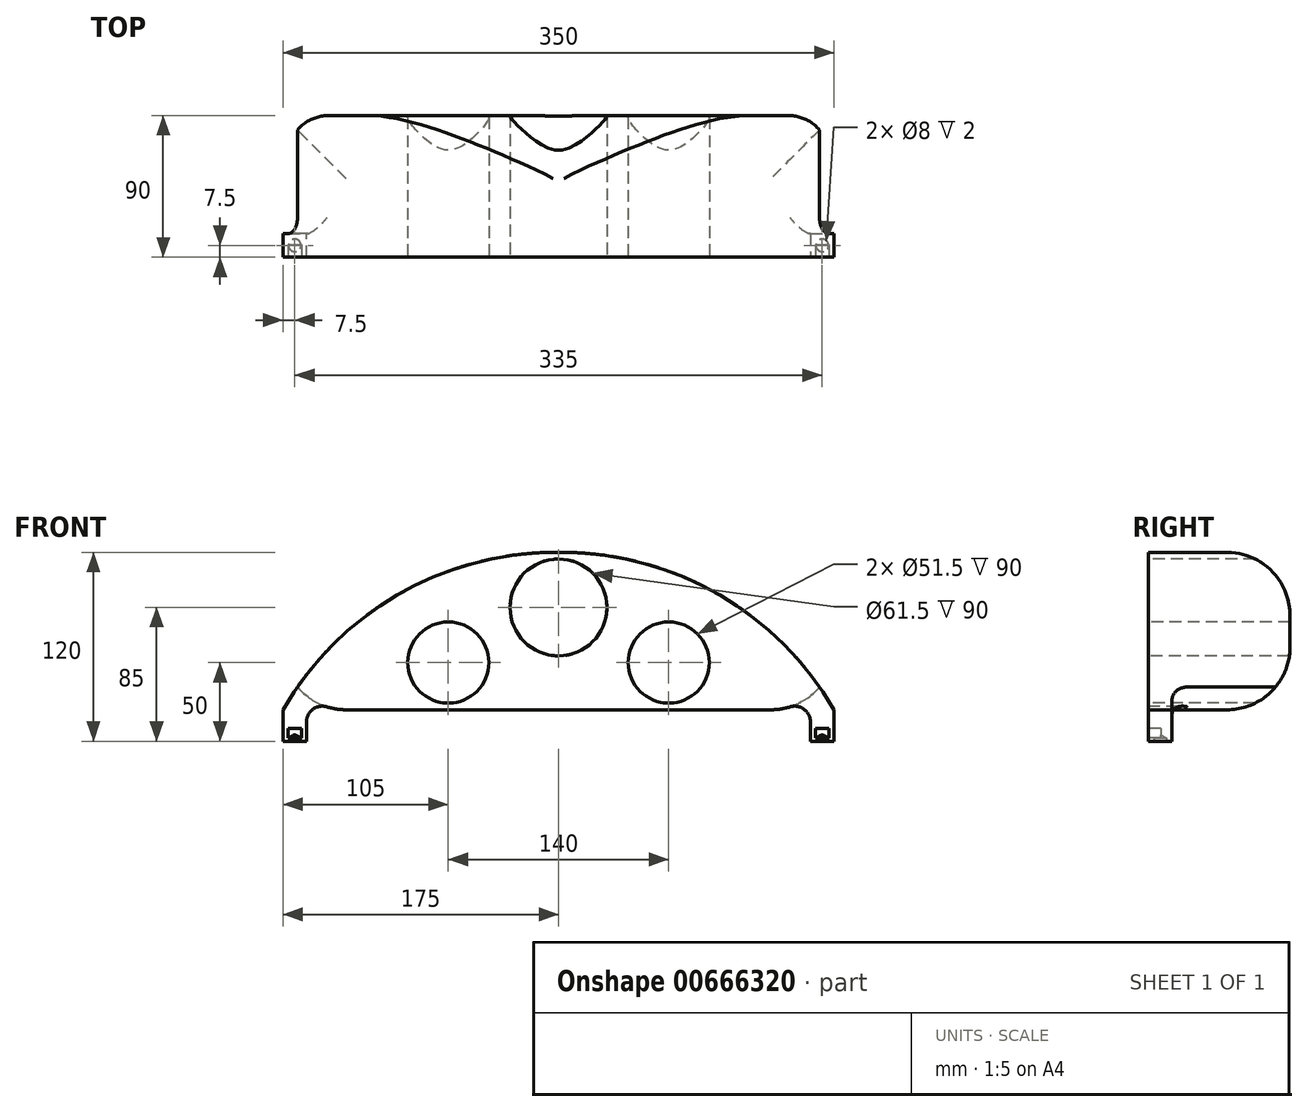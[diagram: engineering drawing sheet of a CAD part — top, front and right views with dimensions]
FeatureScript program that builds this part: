
annotation { "Feature Type Name" : "Feature", "Feature Type Description" : "" }
export const myFeature = defineFeature(function(context is Context, id is Id, definition is map)
    precondition{}
    {
        {
            var Q0;
            Q0=qCreatedBy(makeId("Top.planeOp"),FACE);
            var sketch = newSketch(context, id + "F0", { "sketchPlane" : qUnion([Q0])});
            skLineSegment(sketch, "E0.bottom", {"start": v(-175, 0) * mm, "end": v(-190, 0) * mm});
            skLineSegment(sketch, "E0.top", {"start": v(-175, 15) * mm, "end": v(-190, 15) * mm});
            skLineSegment(sketch, "E0.left", {"start": v(-175, 0) * mm, "end": v(-175, 15) * mm});
            skLineSegment(sketch, "E0.right", {"start": v(-190, 0) * mm, "end": v(-190, 15) * mm});
            skLineSegment(sketch, "E1.bottom", {"start": v(145, 0) * mm, "end": v(160, 0) * mm});
            skLineSegment(sketch, "E1.top", {"start": v(145, 15) * mm, "end": v(160, 15) * mm});
            skLineSegment(sketch, "E1.left", {"start": v(145, 0) * mm, "end": v(145, 15) * mm});
            skLineSegment(sketch, "E1.right", {"start": v(160, 0) * mm, "end": v(160, 15) * mm});
            skSolve(sketch);
        }
        {
            var Q0;
            Q0=qSketchRegion(id+"F0",true);
            extrude(context, id + "F1", {"entities" : qUnion([Q0]), "depth" : 20 * mm, "offsetDistance" : 25 * mm});
        }
        {
            var Q0;
            Q0=makeQuery(id+"F1.opExtrude","CAP_FACE",FACE,{"disambiguationData":[OSD([sQuery(id+"F0.wireOp",EDGE,"E0.bottom"),sQuery(id+"F0.wireOp",EDGE,"E0.top"),sQuery(id+"F0.wireOp",EDGE,"E0.left"),sQuery(id+"F0.wireOp",EDGE,"E0.right")])],"isStart":false});
            var sketch = newSketch(context, id + "F2", { "sketchPlane" : qUnion([Q0])});
            skLineSegment(sketch, "E2.bottom", {"start": v(-190, 15) * mm, "end": v(160, 15) * mm});
            skLineSegment(sketch, "E2.top", {"start": v(-190, 0) * mm, "end": v(160, 0) * mm});
            skLineSegment(sketch, "E2.left", {"start": v(-190, 15) * mm, "end": v(-190, 0) * mm});
            skLineSegment(sketch, "E2.right", {"start": v(160, 15) * mm, "end": v(160, 0) * mm});
            skSolve(sketch);
        }
        {
            var Q0;
            Q0=qSketchRegion(id+"F2",true);
            extrude(context, id + "F3", {"entities" : qUnion([Q0]), "depth" : 100 * mm, "offsetDistance" : 25 * mm});
        }
        {
            var Q0;
            Q0=makeQuery(id+"F1.opExtrude","SWEPT_BODY",BODY,{"disambiguationData":[OSD([sQuery(id+"F0.wireOp",EDGE,"E0.bottom"),sQuery(id+"F0.wireOp",EDGE,"E0.top"),sQuery(id+"F0.wireOp",EDGE,"E0.left"),sQuery(id+"F0.wireOp",EDGE,"E0.right")])]});
            var Q1;
            Q1=makeQuery(id+"F3.opExtrude","SWEPT_BODY",BODY,{"disambiguationData":[OSD([sQuery(id+"F2.wireOp",EDGE,"E2.bottom"),sQuery(id+"F2.wireOp",EDGE,"E2.top"),sQuery(id+"F2.wireOp",EDGE,"E2.left"),sQuery(id+"F2.wireOp",EDGE,"E2.right")])]});
            var Q2;
            Q2=makeQuery(id+"F1.opExtrude","SWEPT_BODY",BODY,{"disambiguationData":[OSD([sQuery(id+"F0.wireOp",EDGE,"E1.bottom"),sQuery(id+"F0.wireOp",EDGE,"E1.top"),sQuery(id+"F0.wireOp",EDGE,"E1.left"),sQuery(id+"F0.wireOp",EDGE,"E1.right")])]});
            booleanBodies(context, id + "F4", {"operationType" : BooleanOperationType.UNION, "tools" : qUnion([Q0, Q1, Q2])});
        }
        {
            var Q0;
            Q0=makeQuery(id+"F4.opBoolean","MERGE",FACE,{"derivedFrom":[makeQuery(id+"F1.opExtrude","SWEPT_FACE",FACE,{"disambiguationData":[OSD([sQuery(id+"F0.wireOp",EDGE,"E0.bottom")])]}),makeQuery(id+"F1.opExtrude","SWEPT_FACE",FACE,{"disambiguationData":[OSD([sQuery(id+"F0.wireOp",EDGE,"E1.bottom")])]}),makeQuery(id+"F3.opExtrude","SWEPT_FACE",FACE,{"disambiguationData":[OSD([sQuery(id+"F2.wireOp",EDGE,"E2.top")])]})]});
            var sketch = newSketch(context, id + "F5", { "sketchPlane" : qUnion([Q0])});
            skPoint(sketch, "E3", {"position": v(-15, 85) * mm});
            skPoint(sketch, "E3.positionSnap0", {"position": v(-15, 20) * mm});
            skPoint(sketch, "E4", {"position": v(-85, 50) * mm});
            skPoint(sketch, "E5", {"position": v(55, 50) * mm});
            skCircle(sketch, "E6", {"center": v(-15, 85) * mm, "radius": 30.75 * mm});
            skCircle(sketch, "E7", {"center": v(55, 50) * mm, "radius": 25.75 * mm});
            skCircle(sketch, "E8", {"center": v(-85, 50) * mm, "radius": 25.75 * mm});
            skArc(sketch, "E9", {"start": v(-15, 120) * mm, "mid": v(-116.02, 93.66) * mm, "end": v(-190, 20) * mm});
            skArc(sketch, "E10", {"start": v(160, 20) * mm, "mid": v(86.02, 93.66) * mm, "end": v(-15, 120) * mm});
            skSolve(sketch);
        }
        {
            var Q0;
            Q0=qSketchRegion(id+"F5",true);
            extrude(context, id + "F6", {"entities" : qUnion([Q0]), "operationType" : NewBodyOperationType.REMOVE, "oppositeDirection" : true, "depth" : 25 * mm, "offsetDistance" : 25 * mm});
        }
        {
            var Q0;
            Q0=qSketchRegion(id+"F5",true);
            extrude(context, id + "F7", {"entities" : qUnion([Q0]), "operationType" : NewBodyOperationType.REMOVE, "oppositeDirection" : true, "depth" : 25 * mm, "offsetDistance" : 25 * mm});
        }
        {
            var Q0;
            Q0=makeQuery(id+"F4.opBoolean","MERGE",FACE,{"derivedFrom":[makeQuery(id+"F1.opExtrude","SWEPT_FACE",FACE,{"disambiguationData":[OSD([sQuery(id+"F0.wireOp",EDGE,"E0.top")])]}),makeQuery(id+"F1.opExtrude","SWEPT_FACE",FACE,{"disambiguationData":[OSD([sQuery(id+"F0.wireOp",EDGE,"E1.top")])]}),makeQuery(id+"F3.opExtrude","SWEPT_FACE",FACE,{"disambiguationData":[OSD([sQuery(id+"F2.wireOp",EDGE,"E2.bottom")])]})]});
            var sketch = newSketch(context, id + "F8", { "sketchPlane" : qUnion([Q0])});
            skLineSegment(sketch, "E11", {"start": v(-145, 20) * mm, "end": v(-160, 20) * mm});
            skLineSegment(sketch, "E12", {"start": v(175, 20) * mm, "end": v(190, 20) * mm});
            skSolve(sketch);
        }
        {
            var Q0;
            {var subQ7=sQuery(id+"F8.wireOp",EDGE,"E11");Q0=makeQuery(id+"F8.imprint","IMPRINT",FACE,{"disambiguationData":[TD([[makeQuery(id+"F8.imprint","IMPRINT",EDGE,{"derivedFrom":subQ7}),-1.0]])]});}
            extrude(context, id + "F9", {"entities" : qUnion([Q0]), "operationType" : NewBodyOperationType.ADD, "depth" : 75 * mm, "offsetDistance" : 25 * mm});
        }
        {
            var Q0;
            {var subQ0=sQuery(id+"F2.wireOp",EDGE,"E2.right");Q0=makeQuery(id+"F9.boolean.opBoolean","MERGE",EDGE,{"derivedFrom":[makeQuery(id+"F3.opExtrude","CAP_EDGE",EDGE,{"disambiguationData":[OSD([subQ0])],"isStart":false}),makeQuery(id+"F9.opExtrude","SWEPT_EDGE",EDGE,{"disambiguationData":[OSD([sQuery(id+"F0.wireOp",EDGE,"E1.top"),sQuery(id+"F0.wireOp",EDGE,"E1.right"),sQuery(id+"F2.wireOp",EDGE,"E2.bottom"),subQ0])]})]});}
            var Q1;
            {var subQ0=sQuery(id+"F2.wireOp",EDGE,"E2.left");Q1=makeQuery(id+"F9.boolean.opBoolean","MERGE",EDGE,{"derivedFrom":[makeQuery(id+"F3.opExtrude","CAP_EDGE",EDGE,{"disambiguationData":[OSD([subQ0])],"isStart":false}),makeQuery(id+"F9.opExtrude","SWEPT_EDGE",EDGE,{"disambiguationData":[OSD([sQuery(id+"F0.wireOp",EDGE,"E0.top"),sQuery(id+"F0.wireOp",EDGE,"E0.right"),sQuery(id+"F2.wireOp",EDGE,"E2.bottom"),subQ0])]})]});}
            var Q2;
            Q2=makeQuery(id+"F9.opExtrude","SWEPT_EDGE",EDGE,{"disambiguationData":[OSD([sQuery(id+"F0.wireOp",EDGE,"E0.top"),sQuery(id+"F0.wireOp",EDGE,"E0.right"),sQuery(id+"F2.wireOp",EDGE,"E2.bottom"),sQuery(id+"F2.wireOp",EDGE,"E2.left"),sQuery(id+"F8.wireOp",EDGE,"E12")])]});
            var Q3;
            Q3=makeQuery(id+"F9.opExtrude","SWEPT_EDGE",EDGE,{"disambiguationData":[OSD([sQuery(id+"F0.wireOp",EDGE,"E1.top"),sQuery(id+"F0.wireOp",EDGE,"E1.right"),sQuery(id+"F2.wireOp",EDGE,"E2.bottom"),sQuery(id+"F2.wireOp",EDGE,"E2.right"),sQuery(id+"F8.wireOp",EDGE,"E11")])]});
            var Q4;
            Q4=makeQuery(id+"F9.opExtrude","CAP_EDGE",EDGE,{"disambiguationData":[OSD([sQuery(id+"F2.wireOp",EDGE,"E2.bottom")])],"isStart":false});
            var Q5;
            Q5=makeQuery(id+"F9.opExtrude","CAP_EDGE",EDGE,{"disambiguationData":[OSD([sQuery(id+"F2.wireOp",EDGE,"E2.bottom"),sQuery(id+"F8.wireOp",EDGE,"E11"),sQuery(id+"F8.wireOp",EDGE,"E12")])],"isStart":false});
            fillet(context, id + "F10", {"entities" : qUnion([Q0, Q1, Q2, Q3, Q4, Q5]), "radius" : 40 * mm, "tangentPropagation" : true, "allowEdgeOverflow" : false});
        }
        {
            var Q0;
            {var subQ0=sQuery(id+"F0.wireOp",EDGE,"E0.right");var subQ1=sQuery(id+"F2.wireOp",EDGE,"E2.left");var subQ2=sQuery(id+"F2.wireOp",EDGE,"E2.bottom");var subQ3=sQuery(id+"F0.wireOp",EDGE,"E0.left");var subQ4=sQuery(id+"F0.wireOp",EDGE,"E0.top");var subQ5=sQuery(id+"F8.wireOp",EDGE,"E12");Q0=makeQuery(id+"F10.opFillet","BLEND_EDGE",EDGE,{"blendedFrom":[makeQuery(id+"F9.opExtrude","SWEPT_EDGE",EDGE,{"disambiguationData":[OSD([subQ4,subQ0,subQ2,subQ1,subQ5])]}),makeQuery(id+"F9.boolean.opBoolean","SPLIT",FACE,{"disambiguationData":[TD([makeQuery(id+"F1.opExtrude","SWEPT_FACE",FACE,{"disambiguationData":[OSD([subQ3])]})])],"derivedFrom":makeQuery(id+"F4.opBoolean","MERGE",FACE,{"derivedFrom":[makeQuery(id+"F1.opExtrude","SWEPT_FACE",FACE,{"disambiguationData":[OSD([subQ4])]}),makeQuery(id+"F1.opExtrude","SWEPT_FACE",FACE,{"disambiguationData":[OSD([sQuery(id+"F0.wireOp",EDGE,"E1.top")])]}),makeQuery(id+"F3.opExtrude","SWEPT_FACE",FACE,{"disambiguationData":[OSD([subQ2])]})]})})],"blendedInto":[makeQuery(id+"F9.boolean.opBoolean","SPLIT",FACE,{"disambiguationData":[TD([makeQuery(id+"F1.opExtrude","SWEPT_FACE",FACE,{"disambiguationData":[OSD([subQ3])]})])],"derivedFrom":makeQuery(id+"F4.opBoolean","MERGE",FACE,{"derivedFrom":[makeQuery(id+"F1.opExtrude","SWEPT_FACE",FACE,{"disambiguationData":[OSD([subQ4])]}),makeQuery(id+"F1.opExtrude","SWEPT_FACE",FACE,{"disambiguationData":[OSD([sQuery(id+"F0.wireOp",EDGE,"E1.top")])]}),makeQuery(id+"F3.opExtrude","SWEPT_FACE",FACE,{"disambiguationData":[OSD([subQ2])]})]})})]});}
            var Q1;
            Q1=makeQuery(id+"F10.opFillet","BLEND_EDGE",EDGE,{"blendedFrom":[makeQuery(id+"F9.opExtrude","SWEPT_EDGE",EDGE,{"disambiguationData":[OSD([sQuery(id+"F0.wireOp",EDGE,"E0.top"),sQuery(id+"F0.wireOp",EDGE,"E0.right"),sQuery(id+"F2.wireOp",EDGE,"E2.bottom"),sQuery(id+"F2.wireOp",EDGE,"E2.left"),sQuery(id+"F8.wireOp",EDGE,"E12")])]}),makeQuery(id+"F1.opExtrude","SWEPT_FACE",FACE,{"disambiguationData":[OSD([sQuery(id+"F0.wireOp",EDGE,"E0.left")])]})],"blendedInto":[makeQuery(id+"F1.opExtrude","SWEPT_FACE",FACE,{"disambiguationData":[OSD([sQuery(id+"F0.wireOp",EDGE,"E0.left")])]})]});
            var Q2;
            Q2=makeQuery(id+"F10.opFillet","BLEND_EDGE",EDGE,{"blendedFrom":[makeQuery(id+"F9.opExtrude","SWEPT_EDGE",EDGE,{"disambiguationData":[OSD([sQuery(id+"F0.wireOp",EDGE,"E1.top"),sQuery(id+"F0.wireOp",EDGE,"E1.right"),sQuery(id+"F2.wireOp",EDGE,"E2.bottom"),sQuery(id+"F2.wireOp",EDGE,"E2.right"),sQuery(id+"F8.wireOp",EDGE,"E11")])]}),makeQuery(id+"F1.opExtrude","SWEPT_FACE",FACE,{"disambiguationData":[OSD([sQuery(id+"F0.wireOp",EDGE,"E1.left")])]})],"blendedInto":[makeQuery(id+"F1.opExtrude","SWEPT_FACE",FACE,{"disambiguationData":[OSD([sQuery(id+"F0.wireOp",EDGE,"E1.left")])]})]});
            var Q3;
            {var subQ0=sQuery(id+"F2.wireOp",EDGE,"E2.right");var subQ1=sQuery(id+"F2.wireOp",EDGE,"E2.bottom");var subQ2=sQuery(id+"F0.wireOp",EDGE,"E1.right");var subQ3=sQuery(id+"F0.wireOp",EDGE,"E1.left");var subQ4=sQuery(id+"F0.wireOp",EDGE,"E1.top");var subQ5=sQuery(id+"F8.wireOp",EDGE,"E11");Q3=makeQuery(id+"F10.opFillet","BLEND_EDGE",EDGE,{"blendedFrom":[makeQuery(id+"F9.opExtrude","SWEPT_EDGE",EDGE,{"disambiguationData":[OSD([subQ4,subQ2,subQ1,subQ0,subQ5])]}),makeQuery(id+"F9.boolean.opBoolean","SPLIT",FACE,{"disambiguationData":[TD([makeQuery(id+"F1.opExtrude","SWEPT_FACE",FACE,{"disambiguationData":[OSD([subQ3])]})])],"derivedFrom":makeQuery(id+"F4.opBoolean","MERGE",FACE,{"derivedFrom":[makeQuery(id+"F1.opExtrude","SWEPT_FACE",FACE,{"disambiguationData":[OSD([sQuery(id+"F0.wireOp",EDGE,"E0.top")])]}),makeQuery(id+"F1.opExtrude","SWEPT_FACE",FACE,{"disambiguationData":[OSD([subQ4])]}),makeQuery(id+"F3.opExtrude","SWEPT_FACE",FACE,{"disambiguationData":[OSD([subQ1])]})]})})],"blendedInto":[makeQuery(id+"F9.boolean.opBoolean","SPLIT",FACE,{"disambiguationData":[TD([makeQuery(id+"F1.opExtrude","SWEPT_FACE",FACE,{"disambiguationData":[OSD([subQ3])]})])],"derivedFrom":makeQuery(id+"F4.opBoolean","MERGE",FACE,{"derivedFrom":[makeQuery(id+"F1.opExtrude","SWEPT_FACE",FACE,{"disambiguationData":[OSD([sQuery(id+"F0.wireOp",EDGE,"E0.top")])]}),makeQuery(id+"F1.opExtrude","SWEPT_FACE",FACE,{"disambiguationData":[OSD([subQ4])]}),makeQuery(id+"F3.opExtrude","SWEPT_FACE",FACE,{"disambiguationData":[OSD([subQ1])]})]})})]});}
            fillet(context, id + "F11", {"entities" : qUnion([Q0, Q1, Q2, Q3]), "radius" : 10 * mm, "tangentPropagation" : true, "allowEdgeOverflow" : false});
        }
        {
            var Q0;
            Q0=makeQuery(id+"F4.opBoolean","MERGE",FACE,{"derivedFrom":[makeQuery(id+"F1.opExtrude","SWEPT_FACE",FACE,{"disambiguationData":[OSD([sQuery(id+"F0.wireOp",EDGE,"E0.bottom")])]}),makeQuery(id+"F1.opExtrude","SWEPT_FACE",FACE,{"disambiguationData":[OSD([sQuery(id+"F0.wireOp",EDGE,"E1.bottom")])]}),makeQuery(id+"F3.opExtrude","SWEPT_FACE",FACE,{"disambiguationData":[OSD([sQuery(id+"F2.wireOp",EDGE,"E2.top")])]})]});
            var sketch = newSketch(context, id + "F12", { "sketchPlane" : qUnion([Q0])});
            skLineSegment(sketch, "E13.bottom", {"start": v(-186.75, 8) * mm, "end": v(-178.25, 8) * mm});
            skLineSegment(sketch, "E13.top", {"start": v(-186.75, 2) * mm, "end": v(-178.25, 2) * mm});
            skLineSegment(sketch, "E13.left", {"start": v(-186.75, 8) * mm, "end": v(-186.75, 2) * mm});
            skLineSegment(sketch, "E13.right", {"start": v(-178.25, 8) * mm, "end": v(-178.25, 2) * mm});
            skLineSegment(sketch, "E14.bottom", {"start": v(148.25, 8) * mm, "end": v(156.75, 8) * mm});
            skLineSegment(sketch, "E14.top", {"start": v(148.25, 2) * mm, "end": v(156.75, 2) * mm});
            skLineSegment(sketch, "E14.left", {"start": v(148.25, 8) * mm, "end": v(148.25, 2) * mm});
            skLineSegment(sketch, "E14.right", {"start": v(156.75, 8) * mm, "end": v(156.75, 2) * mm});
            skSolve(sketch);
        }
        {
            var Q0;
            Q0=qSketchRegion(id+"F12",true);
            extrude(context, id + "F13", {"entities" : qUnion([Q0]), "operationType" : NewBodyOperationType.REMOVE, "oppositeDirection" : true, "depth" : 8 * mm, "offsetDistance" : 25 * mm});
        }
        {
            var Q0;
            Q0=makeQuery(id+"F1.opExtrude","CAP_FACE",FACE,{"disambiguationData":[OSD([sQuery(id+"F0.wireOp",EDGE,"E0.bottom"),sQuery(id+"F0.wireOp",EDGE,"E0.top"),sQuery(id+"F0.wireOp",EDGE,"E0.left"),sQuery(id+"F0.wireOp",EDGE,"E0.right")])],"isStart":true});
            var sketch = newSketch(context, id + "F14", { "sketchPlane" : qUnion([Q0])});
            skPoint(sketch, "E15", {"position": v(-182.5, -7.5) * mm});
            skPoint(sketch, "E15.positionSnap0", {"position": v(-175, -7.5) * mm});
            skPoint(sketch, "E15.positionSnap1", {"position": v(-182.5, 0) * mm});
            skSolve(sketch);
        }
        {
            var Q0;
            Q0=makeQuery(id+"F1.opExtrude","CAP_FACE",FACE,{"disambiguationData":[OSD([sQuery(id+"F0.wireOp",EDGE,"E1.bottom"),sQuery(id+"F0.wireOp",EDGE,"E1.top"),sQuery(id+"F0.wireOp",EDGE,"E1.left"),sQuery(id+"F0.wireOp",EDGE,"E1.right")])],"isStart":true});
            var sketch = newSketch(context, id + "F15", { "sketchPlane" : qUnion([Q0])});
            skPoint(sketch, "E16", {"position": v(152.5, -7.5) * mm});
            skPoint(sketch, "E16.positionSnap0", {"position": v(160, -7.5) * mm});
            skPoint(sketch, "E16.positionSnap1", {"position": v(152.5, 0) * mm});
            skSolve(sketch);
        }
        {
            var Q0;
            Q0=sQuery(id+"F15.wireOp",VERTEX,"E16");
            var Q1;
            Q1=sQuery(id+"F14.wireOp",VERTEX,"E15");
            var Q2;
            Q2=makeQuery(id+"F1.opExtrude","SWEPT_BODY",BODY,{"disambiguationData":[OSD([sQuery(id+"F0.wireOp",EDGE,"E0.bottom"),sQuery(id+"F0.wireOp",EDGE,"E0.top"),sQuery(id+"F0.wireOp",EDGE,"E0.left"),sQuery(id+"F0.wireOp",EDGE,"E0.right")])]});
            hole(context, id + "F16", {"style" : HoleStyle.SIMPLE, "endStyle" : HoleEndStyle.BLIND, "holeDiameter" : 8 * mm, "majorDiameter" : 5 * mm, "holeDepth" : 2 * mm, "isTappedThrough" : true, "tappedDepth" : 12 * mm, "tapClearance" : 3, "startFromSketch" : true, "locations" : qUnion([Q0, Q1]), "scope" : qUnion([Q2])});
        }
        {
            var Q0;
            {var subQ0=sQuery(id+"F5.wireOp",EDGE,"E9");Q0=makeQuery(id+"F5.imprint","IMPRINT",FACE,{"disambiguationData":[TD([[makeQuery(id+"F5.imprint","IMPRINT",EDGE,{"derivedFrom":subQ0}),-1.0]])]});}
            var Q1;
            {var subQ0=sQuery(id+"F5.wireOp",EDGE,"E10");Q1=makeQuery(id+"F5.imprint","IMPRINT",FACE,{"disambiguationData":[TD([[makeQuery(id+"F5.imprint","IMPRINT",EDGE,{"derivedFrom":subQ0}),-1.0]])]});}
            extrude(context, id + "F17", {"entities" : qUnion([Q0, Q1]), "operationType" : NewBodyOperationType.REMOVE, "oppositeDirection" : true, "depth" : 200 * mm, "offsetDistance" : 25 * mm});
        }
    });
